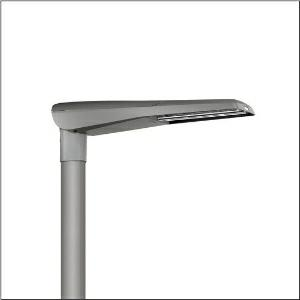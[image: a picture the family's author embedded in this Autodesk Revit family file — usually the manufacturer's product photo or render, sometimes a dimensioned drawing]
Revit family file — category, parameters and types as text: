
# Revit family: streetlight_sl_11_iq_mini___st1_0ab_5xc2nc1f08he_e776
name_source: partatom
category: Lighting Fixtures
units: mm (PartAtom-declared; Revit-internal decimal feet)

## family parameters
Cut with Voids When Loaded = No
Host = Face
Light Source = No
Part Type = Normal
Room Calculation Point = No
Round Connector Dimension = Use Diameter
Shared = No

## types (1)
- --- (1 x LED, 5460 lm, 63.6 W, 2200K)
    Apparent Load = 64 VA
    CIE Flux Codes = 29 63 95 100 100
    Color Rendering = 70
    Color Temperature = 2200K
    Default Elevation = 1800 mm
    Description = Streetlight SL 11 iQ mini, mast luminaire, primary light control with 3 zone facetted reflector, of plastic, silver coated, highly specular, primary optical cover: cover, of PMMA, transparent, light distribution: ST1.0aB, light emission: direct distribution, primary light characteristic: asymmetric, installation type: post-top, side-entry, lamps: LED, High Power LED, rated values: 6.670lm | 62,2W | 107,2lm/W (begin service life); end service life: 6.670lm | 65,6W; at 50% lumin. flux: 3.335lm | 29,4W | 113,4lm/W, colour temperature: 2200/2700/3000/4000K, colour rendering: CRI > 70, light colour: 722/727/730/740, light setting 1 begin service life: 100% | 6.670lm | 62,2W | 107,2lm/W | 3.000K, light setting 1 end service life: 65,6W, further light settings possible, control: Street-Remote, Auto-Match, Temp-Guard, Lumen-Switch, Night-Set, Smart-Wire, Light-Fading, Desk-Remote (wireless, voltage-free reading and setting of iQ features in the workshop via application-optimized NFC function/RFID function), optimised constant luminous flux control (CLO 2.0), with cable H07RN-F 5x 1.5mm², mains connection: 230..240V, AC, 50/60Hz, connection cable pre-assembled, cable length: 8,5m, luminaire housing, of diecast aluminium, powder-coated, Siteco® metallic grey (DB 702S), please order mast flange separately, inclination adjustable without tools: 0°, 5°, 10°, 15° (post-top) | 0°, -5°, -10°, -15° (side-entry), sealing non-destructively replaceable, multi-level sealing system, length: 736mm, width: 174mm, height: 116mm, mast flange for spigot size: 42mm (side-entry): 5XC10008XM4, 60/48mm (side-entry/post-top): 5XC10108XM2, 76/60mm (side-entry/post-top): 5XC10108XM1, equipment: Power, protection rating (complete): IP66, insulation class (complete): insulation class II (safety insulation), certification: CE, ENEC, ENEC+, VDE, impact resistance: IK10, permissible operating ambient temperature for outdoor applications: -25..+50°C, standard-compliant lighting for roads and squares, Environmental Product Declaration (EPD) tested and certified by an independent institute, packaging unit: 1 piece

Light Distribution: ST1.0aB
    Height = 116 mm
    Lamp = 1 x LED
    Lamp Light Flux = 5460 lm
    Lamp Power = 63.6 W
    Lamp count = 1
    Length = 736 mm
    Luminous efficacy = 86 lm/W
    Manufacturer = Siteco
    ModVariant = No
    Model = 5XC2NC1F08HE
    Number of Poles = 1
    OnlyDefault = Yes
    Power Factor = 1
    Product Name = Streetlight SL 11 iQ mini | ST1.0aB
    Product group = mast luminaire | pylon top
    ProductGroupID = 6100
    Protection Class = Protection class II
    Protection Degree = IP 66
    RLX_Detail_Level = 1
    RLX_Emergency_Light_Flux = 0 lm
    RLX_Emergency_Type = 0
    RLX_Emergency_Type_DB = No
    RlxData = <blob elided: 35061 chars, md5=a6b51d06>
    Socket = socket
    Standby Power = 0 W
    System Light Flux = 5460 lm
    System Power = 64 W
    Type Comments = individual setting: luminous flux: 100 % | dim-lin: 254 | 866 mA
    Type Image = l_1003508.jpg
    URL = http://relux.com
    VarID = @adj_002621
    Voltage = 0 V
    Weight = 0.00 kg
    Width = 174 mm

## geometry (parser evidence)
native form markers: Blend x4, Sweep x10
no freeform markers — native parametric forms only
